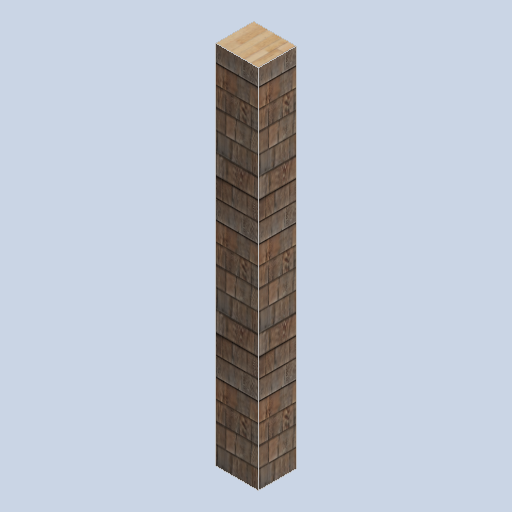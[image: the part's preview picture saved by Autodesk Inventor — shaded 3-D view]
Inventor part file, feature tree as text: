
AUTODESK INVENTOR PART (.ipt)
format: ipt  version: 2024.2 (Build 282272000, 272)  size: 168,960 bytes
history: native  units: in
note: dims shown in document units (in); Inventor stores cm internally (conversion verified against a paired STEP export)
features: other x3, sketch x1
ambient origin geometry x8: Origin, YZ Plane, XZ Plane, XY Plane, X Axis, Y Axis, Z Axis, Center Point
bodies: Solid1 (feature_tree)
feature tree (4):
  other  "support_column_01_MIR2.ipt"
  other  "Solid1::support_column_01_MIR2.ipt"
  other  "TaggingFeature1"
  sketch  "Sketch1"  dims[d0=0.3937in]
